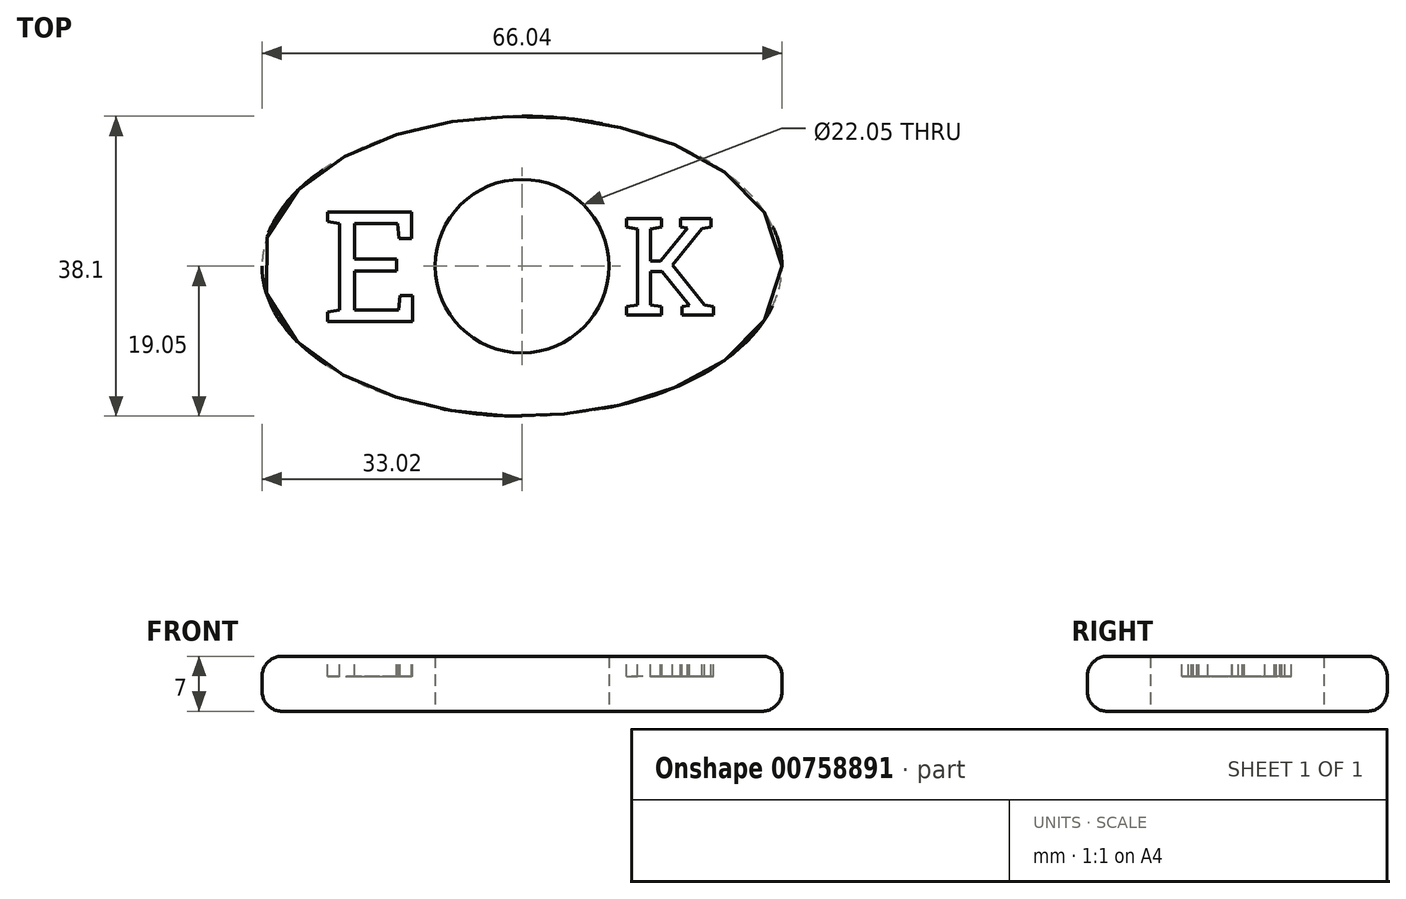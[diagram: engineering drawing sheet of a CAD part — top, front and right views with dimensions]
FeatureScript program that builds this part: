
annotation { "Feature Type Name" : "Feature", "Feature Type Description" : "" }
export const myFeature = defineFeature(function(context is Context, id is Id, definition is map)
    precondition{}
    {
        {
            var Q0;
            Q0=qCreatedBy(makeId("Top.planeOp"),FACE);
            var sketch = newSketch(context, id + "F0", { "sketchPlane" : qUnion([Q0])});
            skEllipse(sketch, "E0", {"center": v(0, 0) * mm, "majorRadius": 33.02 * mm, "minorRadius": 19.05 * mm, "majorAxis": v(1, 0)});
            skCircle(sketch, "E1", {"center": v(0, 0) * mm, "radius": 11.03 * mm});
            skLineSegment(sketch, "E2", {"start": v(-33.02, 0) * mm, "end": v(33.02, 0) * mm, "construction": true});
            skLineSegment(sketch, "E3", {"start": v(0, 19.05) * mm, "end": v(0, -19.05) * mm, "construction": true});
            skSolve(sketch);
        }
        {
            var Q0;
            Q0=makeQuery(id+"F0.imprint","IMPRINT",FACE,{"disambiguationData":[TD([[makeQuery(id+"F0.imprint","IMPRINT",EDGE,{"derivedFrom":sQuery(id+"F0.wireOp",EDGE,"E0")}),1.0]])]});
            extrude(context, id + "F1", {"entities" : qUnion([Q0]), "depth" : 7 * mm, "offsetDistance" : 25.4 * mm});
        }
        {
            var Q0;
            Q0=makeQuery(id+"F1.opExtrude","CAP_EDGE",EDGE,{"disambiguationData":[OSD([sQuery(id+"F0.wireOp",EDGE,"E0")])],"isStart":false});
            var Q1;
            Q1=makeQuery(id+"F1.opExtrude","CAP_EDGE",EDGE,{"disambiguationData":[OSD([sQuery(id+"F0.wireOp",EDGE,"E0")])],"isStart":true});
            fillet(context, id + "F2", {"entities" : qUnion([Q0, Q1]), "radius" : 2.54 * mm, "tangentPropagation" : true, "allowEdgeOverflow" : false});
        }
        {
            var Q0;
            Q0=makeQuery(id+"F1.opExtrude","CAP_FACE",FACE,{"disambiguationData":[OSD([sQuery(id+"F0.wireOp",EDGE,"E0"),sQuery(id+"F0.wireOp",EDGE,"E1")])],"isStart":false});
            var sketch = newSketch(context, id + "F3", { "sketchPlane" : qUnion([Q0])});
            skSolve(sketch);
        }
        {
            var Q0;
            {var subQ0=sQuery(id+"F0.wireOp",EDGE,"E1");Q0=makeQuery(id+"F3.imprint","IMPRINT",FACE,{"disambiguationData":[TD([[makeQuery(id+"F3.imprint","IMPRINT",EDGE,{"derivedFrom":makeQuery(id+"F1.opExtrude","CAP_EDGE",EDGE,{"disambiguationData":[OSD([subQ0])],"isStart":false})}),-1.0]])]});}
            var sketch = newSketch(context, id + "F4", { "sketchPlane" : qUnion([Q0])});
            skText(sketch, "E4", { "text": "E", "fontName": "RobotoSlab-Regular.ttf"});
            skText(sketch, "E5", { "text": "K", "fontName": "RobotoSlab-Regular.ttf"});
            skLineSegment(sketch, "E6", {"start": v(0, 0) * mm, "end": v(-25.4, 0) * mm, "construction": true});
            skLineSegment(sketch, "E7", {"start": v(0, 0) * mm, "end": v(25.4, 0) * mm, "construction": true});
            skLineSegment(sketch, "E8", {"start": v(-25.4, 0) * mm, "end": v(-12.7, 0) * mm, "construction": true});
            skLineSegment(sketch, "E9", {"start": v(12.7, 0) * mm, "end": v(25.4, 0) * mm});
            skPoint(sketch, "E10", {"position": v(19.05, 0) * mm});
            skLineSegment(sketch, "E11", {"start": v(12.7, 0) * mm, "end": v(25.4, 0) * mm, "construction": true});
            skPoint(sketch, "E12", {"position": v(-19.05, 0) * mm});
            const initialGuessF4  = {"E4": [-0.0254, -0.00706, 1, 0, 0.01411], "E5": [0.0127, -0.0062, 1, 0, 0.0124]};
            skSetInitialGuess(sketch, initialGuessF4);
            skSolve(sketch);
        }
        {
            var Q0;
            Q0=qSketchRegion(id+"F4",true);
            extrude(context, id + "F5", {"entities" : qUnion([Q0]), "operationType" : NewBodyOperationType.REMOVE, "oppositeDirection" : true, "depth" : 2.54 * mm, "offsetDistance" : 25.4 * mm});
        }
    });
